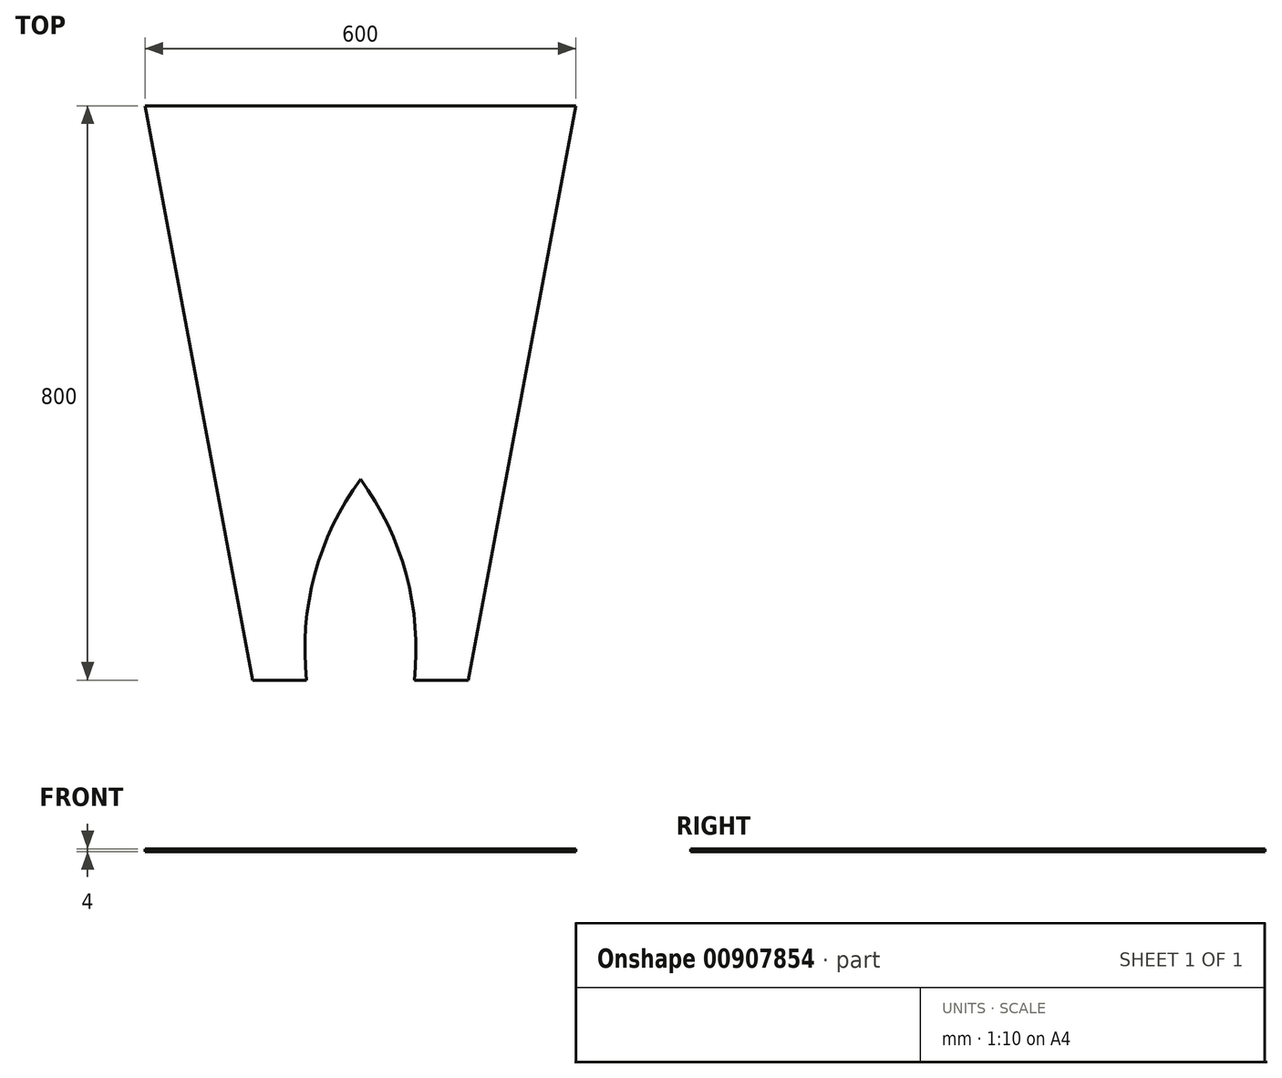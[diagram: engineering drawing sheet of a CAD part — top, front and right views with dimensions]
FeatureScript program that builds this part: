
annotation { "Feature Type Name" : "Feature", "Feature Type Description" : "" }
export const myFeature = defineFeature(function(context is Context, id is Id, definition is map)
    precondition{}
    {
        {
            var Q0;
            Q0=qCreatedBy(makeId("Top.planeOp"),FACE);
            var sketch = newSketch(context, id + "F0", { "sketchPlane" : qUnion([Q0])});
            skLineSegment(sketch, "E0", {"start": v(0, 0) * mm, "end": v(300, 0) * mm});
            skLineSegment(sketch, "E1", {"start": v(0, 0) * mm, "end": v(-300, 0) * mm});
            skLineSegment(sketch, "E2", {"start": v(-300, 0) * mm, "end": v(-300, 700) * mm});
            skLineSegment(sketch, "E3", {"start": v(300, 700) * mm, "end": v(300, 0) * mm});
            skLineSegment(sketch, "E4", {"start": v(0, 0) * mm, "end": v(-150, 0) * mm});
            skLineSegment(sketch, "E5", {"start": v(0, 0) * mm, "end": v(150, 0) * mm});
            skLineSegment(sketch, "E6", {"start": v(-300, 700) * mm, "end": v(-300, 800) * mm});
            skLineSegment(sketch, "E7", {"start": v(-300, 800) * mm, "end": v(300, 800) * mm});
            skLineSegment(sketch, "E8", {"start": v(300, 800) * mm, "end": v(300, 700) * mm});
            skLineSegment(sketch, "E9", {"start": v(-150, 0) * mm, "end": v(-300, 800) * mm});
            skLineSegment(sketch, "E10", {"start": v(150, 0) * mm, "end": v(300, 800) * mm});
            skLineSegment(sketch, "E11", {"start": v(0, 0) * mm, "end": v(0, 280) * mm});
            skLineSegment(sketch, "E12", {"start": v(150, 0) * mm, "end": v(0, 0) * mm});
            skArc(sketch, "E13", {"start": v(0, 280) * mm, "mid": v(-63.76, 147.03) * mm, "end": v(-75, 0) * mm});
            skArc(sketch, "E14", {"start": v(75, 0) * mm, "mid": v(63.76, 147.03) * mm, "end": v(0, 280) * mm});
            skSolve(sketch);
        }
        {
            var Q0;
            Q0=makeQuery(id+"F0.imprint","IMPRINT",FACE,{"disambiguationData":[TD([[makeQuery(id+"F0.imprint","IMPRINT",EDGE,{"derivedFrom":sQuery(id+"F0.wireOp",EDGE,"E7")}),-1.0]])]});
            extrude(context, id + "F1", {"entities" : qUnion([Q0]), "depth" : 4 * mm, "offsetDistance" : 25 * mm});
        }
    });
